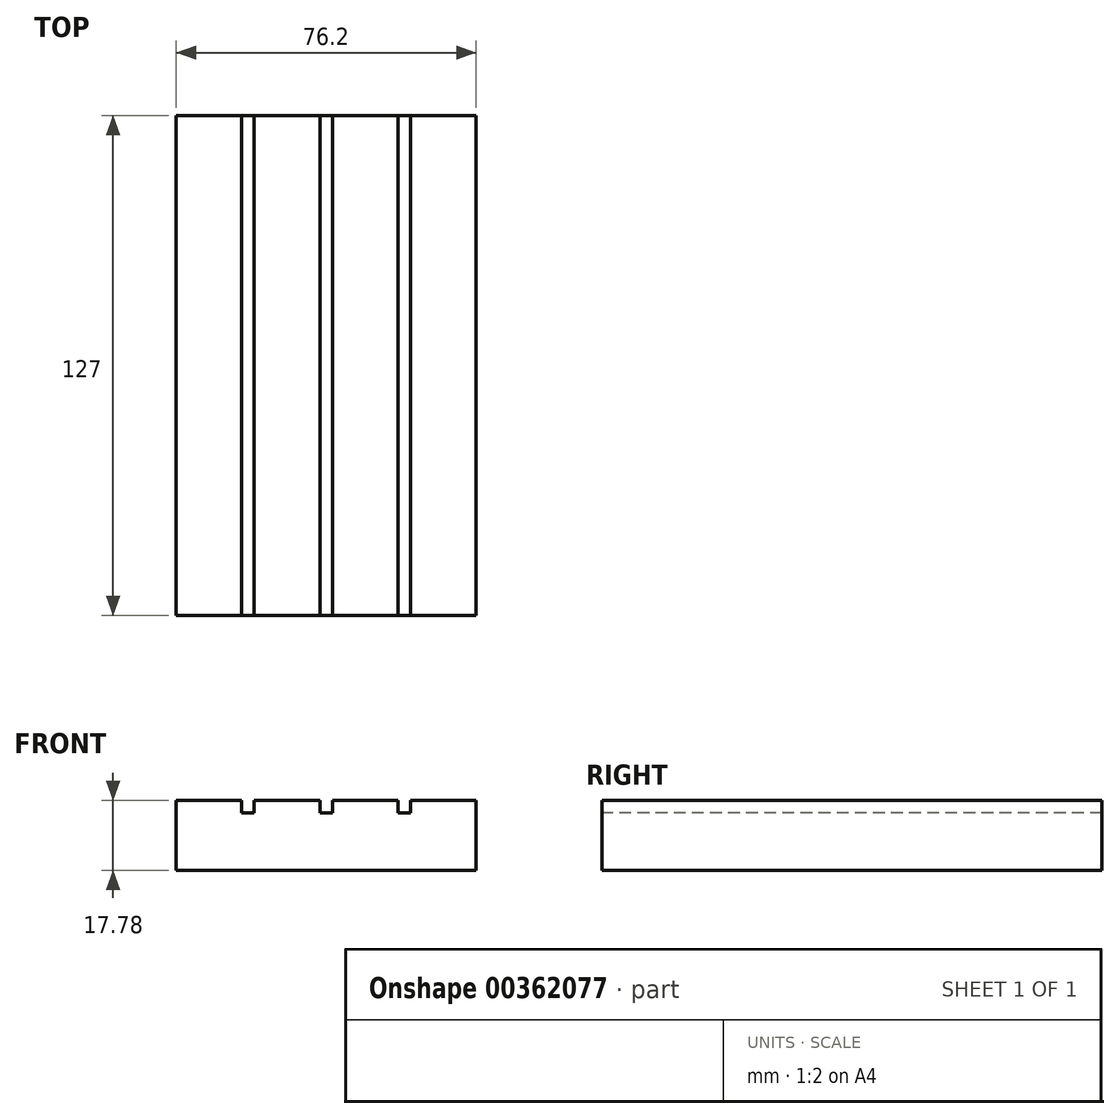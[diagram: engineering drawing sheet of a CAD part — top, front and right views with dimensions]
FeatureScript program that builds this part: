
annotation { "Feature Type Name" : "Feature", "Feature Type Description" : "" }
export const myFeature = defineFeature(function(context is Context, id is Id, definition is map)
    precondition{}
    {
        {
            var Q0;
            Q0=qCreatedBy(makeId("Top.planeOp"),FACE);
            var sketch = newSketch(context, id + "F0", { "sketchPlane" : qUnion([Q0])});
            skLineSegment(sketch, "E0.bottom", {"start": v(38.1, 63.5) * mm, "end": v(-38.1, 63.5) * mm});
            skLineSegment(sketch, "E0.top", {"start": v(38.1, -63.5) * mm, "end": v(-38.1, -63.5) * mm});
            skLineSegment(sketch, "E0.left", {"start": v(38.1, 63.5) * mm, "end": v(38.1, -63.5) * mm});
            skLineSegment(sketch, "E0.right", {"start": v(-38.1, 63.5) * mm, "end": v(-38.1, -63.5) * mm});
            skPoint(sketch, "E0.middle", {"position": v(0, 0) * mm});
            skSolve(sketch);
        }
        {
            var Q0;
            Q0 = qSketchRegion(id + "F0", true);
            extrude(context, id + "F1", {"entities" : qUnion([Q0]), "depth" : 17.78 * mm});
        }
        {
            var Q0;
            Q0=makeQuery(id+"F1.opExtrude","SWEPT_FACE",FACE,{"disambiguationData":[OSD([sQuery(id+"F0.wireOp",EDGE,"E0.top")])]});
            var sketch = newSketch(context, id + "F2", { "sketchPlane" : qUnion([Q0])});
            skLineSegment(sketch, "E1.bottom", {"start": v(-38.1, 17.78) * mm, "end": v(-21.43, 17.78) * mm});
            skLineSegment(sketch, "E1.top", {"start": v(-38.1, 14.6) * mm, "end": v(-21.43, 14.6) * mm});
            skLineSegment(sketch, "E1.left", {"start": v(-38.1, 17.78) * mm, "end": v(-38.1, 14.6) * mm});
            skLineSegment(sketch, "E1.right", {"start": v(-21.43, 17.78) * mm, "end": v(-21.43, 14.6) * mm});
            skLineSegment(sketch, "E2.1.0.0", {"start": v(-18.26, 14.6) * mm, "end": v(-1.59, 14.6) * mm});
            skLineSegment(sketch, "E2.1.0.1", {"start": v(-1.59, 17.78) * mm, "end": v(-1.59, 14.6) * mm});
            skLineSegment(sketch, "E2.1.0.2", {"start": v(-18.26, 17.78) * mm, "end": v(-18.26, 14.6) * mm});
            skLineSegment(sketch, "E2.2.0.0", {"start": v(1.59, 14.6) * mm, "end": v(18.26, 14.6) * mm});
            skLineSegment(sketch, "E2.2.0.1", {"start": v(18.26, 17.78) * mm, "end": v(18.26, 14.6) * mm});
            skLineSegment(sketch, "E2.2.0.2", {"start": v(1.59, 17.78) * mm, "end": v(1.59, 14.6) * mm});
            skLineSegment(sketch, "E2.direction1", {"start": v(-38.1, 14.6) * mm, "end": v(-18.26, 14.6) * mm, "construction": true});
            skLineSegment(sketch, "E3", {"start": v(-21.43, 14.6) * mm, "end": v(-18.26, 14.6) * mm});
            skLineSegment(sketch, "E4", {"start": v(-1.59, 14.6) * mm, "end": v(1.59, 14.6) * mm});
            skLineSegment(sketch, "E5", {"start": v(-1.59, 17.78) * mm, "end": v(1.59, 17.78) * mm});
            skLineSegment(sketch, "E6", {"start": v(-21.43, 17.78) * mm, "end": v(-18.26, 17.78) * mm});
            skLineSegment(sketch, "E7.0.3.0", {"start": v(21.43, 14.6) * mm, "end": v(38.1, 14.6) * mm});
            skLineSegment(sketch, "E7.3.3.0", {"start": v(38.1, 17.78) * mm, "end": v(38.1, 14.6) * mm});
            skLineSegment(sketch, "E7.6.3.0", {"start": v(21.43, 17.78) * mm, "end": v(21.43, 14.6) * mm});
            skLineSegment(sketch, "E8", {"start": v(18.26, 14.6) * mm, "end": v(21.43, 14.6) * mm});
            skLineSegment(sketch, "E9", {"start": v(18.26, 17.78) * mm, "end": v(21.43, 17.78) * mm});
            skSolve(sketch);
        }
        {
            var Q0;
            Q0=makeQuery(id+"F2.imprint","IMPRINT",FACE,{"disambiguationData":[TD([[makeQuery(id+"F2.imprint","IMPRINT",EDGE,{"derivedFrom":sQuery(id+"F2.wireOp",EDGE,"E2.1.0.1")}),1.0]])]});
            var Q1;
            Q1=makeQuery(id+"F2.imprint","IMPRINT",FACE,{"disambiguationData":[TD([[makeQuery(id+"F2.imprint","IMPRINT",EDGE,{"derivedFrom":sQuery(id+"F2.wireOp",EDGE,"E2.2.0.1")}),1.0]])]});
            var Q2;
            Q2=makeQuery(id+"F2.imprint","IMPRINT",FACE,{"disambiguationData":[TD([[makeQuery(id+"F2.imprint","IMPRINT",EDGE,{"derivedFrom":sQuery(id+"F2.wireOp",EDGE,"E1.right")}),1.0]])]});
            extrude(context, id + "F3", {"entities" : qUnion([Q0, Q1, Q2]), "operationType" : NewBodyOperationType.REMOVE, "endBound" : BoundingType.THROUGH_ALL, "oppositeDirection" : true, "depth" : 25.4 * mm});
        }
    });
